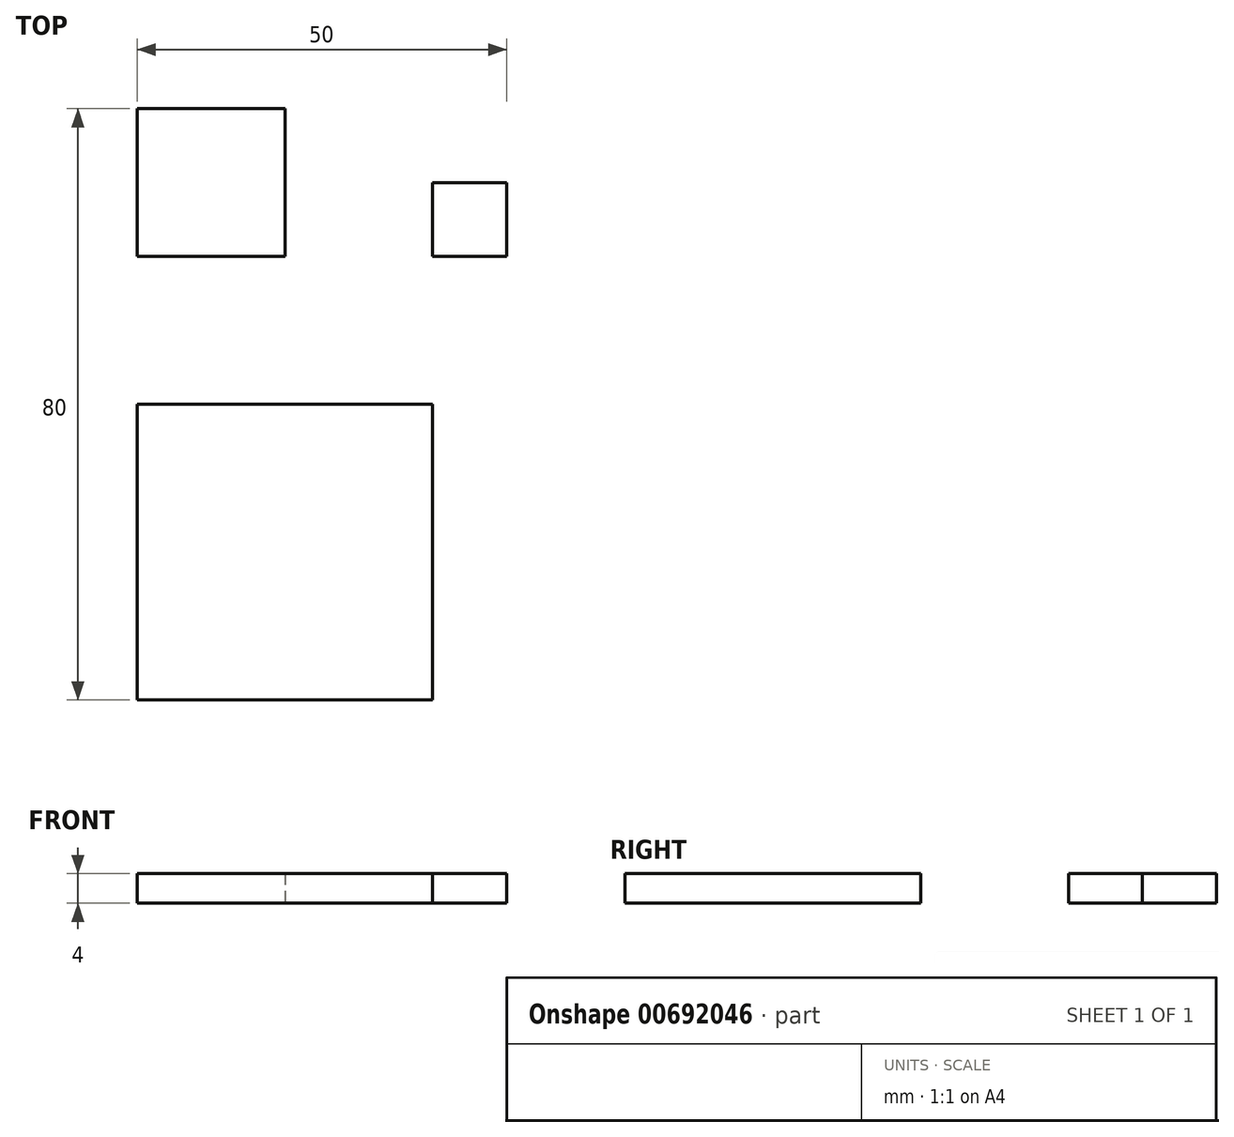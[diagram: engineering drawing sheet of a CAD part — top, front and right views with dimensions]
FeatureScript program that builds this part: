
annotation { "Feature Type Name" : "Feature", "Feature Type Description" : "" }
export const myFeature = defineFeature(function(context is Context, id is Id, definition is map)
    precondition{}
    {
        {
            var Q0;
            Q0=qCreatedBy(makeId("Top.planeOp"),FACE);
            var sketch = newSketch(context, id + "F0", { "sketchPlane" : qUnion([Q0])});
            skLineSegment(sketch, "E0.bottom", {"start": v(0, 0) * mm, "end": v(10, 0) * mm});
            skLineSegment(sketch, "E0.top", {"start": v(0, 10) * mm, "end": v(10, 10) * mm});
            skLineSegment(sketch, "E0.left", {"start": v(0, 0) * mm, "end": v(0, 10) * mm});
            skLineSegment(sketch, "E0.right", {"start": v(10, 0) * mm, "end": v(10, 10) * mm});
            skLineSegment(sketch, "E1.bottom", {"start": v(-40, 0) * mm, "end": v(-20, 0) * mm});
            skLineSegment(sketch, "E1.top", {"start": v(-40, 20) * mm, "end": v(-20, 20) * mm});
            skLineSegment(sketch, "E1.left", {"start": v(-40, 0) * mm, "end": v(-40, 20) * mm});
            skLineSegment(sketch, "E1.right", {"start": v(-20, 0) * mm, "end": v(-20, 20) * mm});
            skLineSegment(sketch, "E2.bottom", {"start": v(-40, -20) * mm, "end": v(0, -20) * mm});
            skLineSegment(sketch, "E2.top", {"start": v(-40, -60) * mm, "end": v(0, -60) * mm});
            skLineSegment(sketch, "E2.left", {"start": v(-40, -20) * mm, "end": v(-40, -60) * mm});
            skLineSegment(sketch, "E2.right", {"start": v(0, -20) * mm, "end": v(0, -60) * mm});
            skSolve(sketch);
        }
        {
            var Q0;
            Q0 = qSketchRegion(id + "F0", true);
            extrude(context, id + "F1", {"entities" : qUnion([Q0]), "depth" : 4 * mm, "offsetDistance" : 25 * mm});
        }
    });
